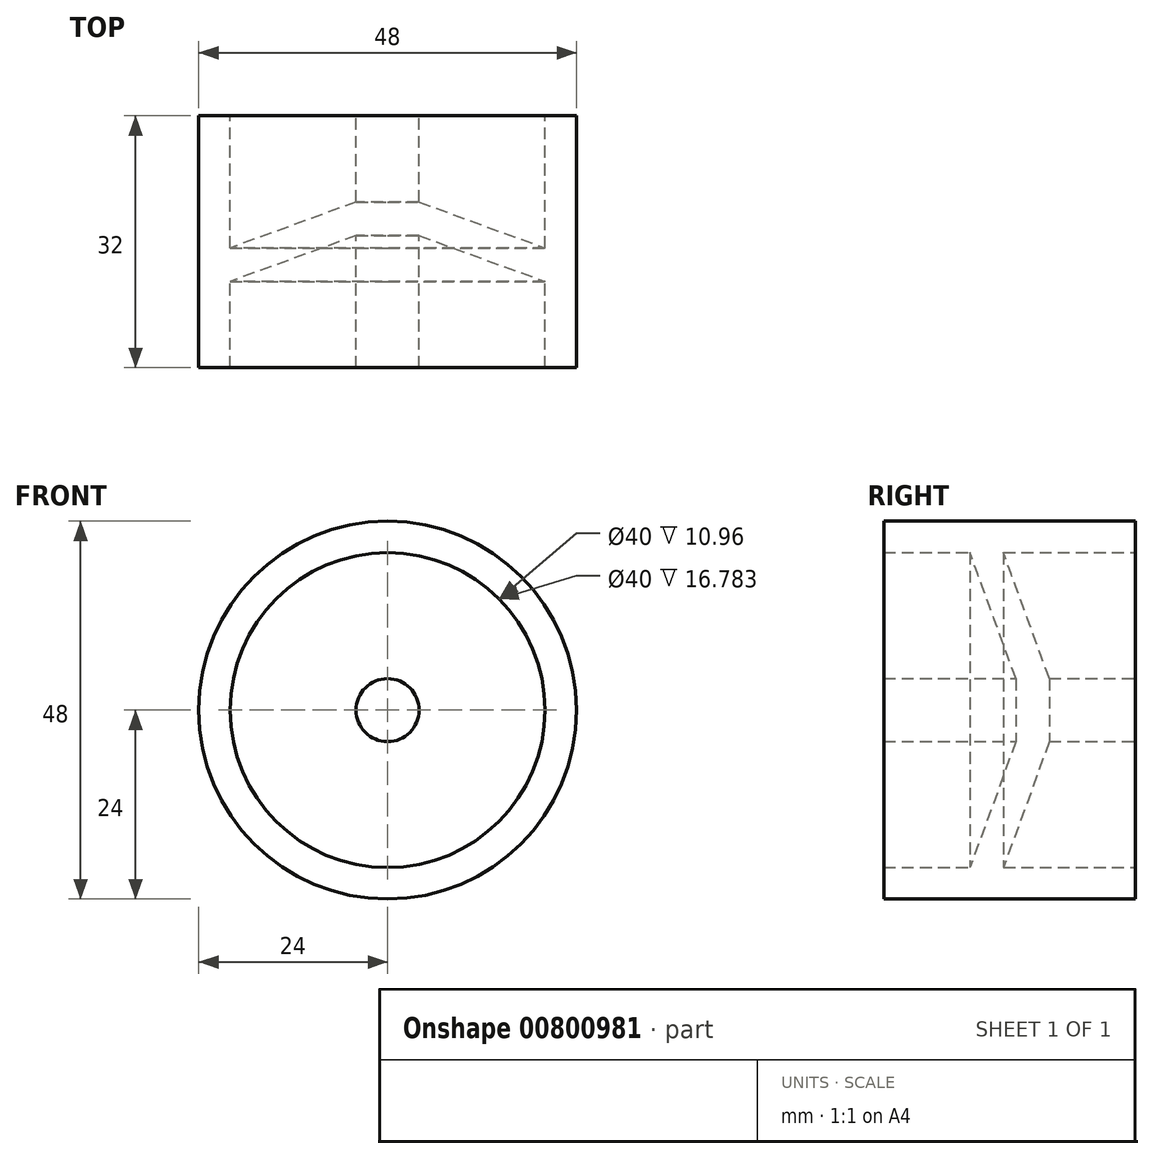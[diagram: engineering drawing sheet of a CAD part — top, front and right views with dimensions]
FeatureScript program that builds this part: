
annotation { "Feature Type Name" : "Feature", "Feature Type Description" : "" }
export const myFeature = defineFeature(function(context is Context, id is Id, definition is map)
    precondition{}
    {
        {
            var Q0;
            Q0=qCreatedBy(makeId("Top.planeOp"),FACE);
            var sketch = newSketch(context, id + "F0", { "sketchPlane" : qUnion([Q0])});
            skLineSegment(sketch, "E0", {"start": v(0, 0) * mm, "end": v(0, -32) * mm});
            skLineSegment(sketch, "E1", {"start": v(0, -32) * mm, "end": v(4, -32) * mm});
            skLineSegment(sketch, "E2", {"start": v(4, -32) * mm, "end": v(4, -15.22) * mm});
            skLineSegment(sketch, "E3", {"start": v(4, -15.22) * mm, "end": v(20, -21.04) * mm});
            skLineSegment(sketch, "E4", {"start": v(20, -21.04) * mm, "end": v(20, -32) * mm});
            skLineSegment(sketch, "E5", {"start": v(20, -32) * mm, "end": v(24, -32) * mm});
            skLineSegment(sketch, "E6", {"start": v(24, -32) * mm, "end": v(24, 0) * mm});
            skLineSegment(sketch, "E7", {"start": v(24, 0) * mm, "end": v(20, 0) * mm});
            skLineSegment(sketch, "E8", {"start": v(20, 0) * mm, "end": v(20, -16.78) * mm});
            skLineSegment(sketch, "E9", {"start": v(20, -16.78) * mm, "end": v(4, -10.96) * mm});
            skLineSegment(sketch, "E10", {"start": v(4, -10.96) * mm, "end": v(4, 0) * mm});
            skLineSegment(sketch, "E11", {"start": v(4, 0) * mm, "end": v(0, 0) * mm});
            skSolve(sketch);
        }
        {
            var Q0;
            Q0=makeQuery(id+"F0.imprint","IMPRINT",FACE,{"disambiguationData":[TD([[makeQuery(id+"F0.imprint","IMPRINT",EDGE,{"derivedFrom":sQuery(id+"F0.wireOp",EDGE,"E0")}),1.0]])]});
            var Q1;
            Q1=sQuery(id+"F0.wireOp",EDGE,"E0");
            revolve(context, id + "F1", {"surfaceOperationType" : NewSurfaceOperationType.NEW, "entities" : qUnion([Q0]), "axis" : qUnion([Q1]), "revolveType" : RevolveType.FULL});
        }
    });
